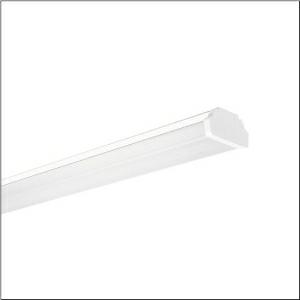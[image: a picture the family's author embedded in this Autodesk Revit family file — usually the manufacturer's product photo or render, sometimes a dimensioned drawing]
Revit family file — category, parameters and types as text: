
# Revit family: dus_31_gen_2_53bd812cv685c2_b411
name_source: partatom
category: Lighting Fixtures
units: mm (PartAtom-declared; Revit-internal decimal feet)

## family parameters
Cut with Voids When Loaded = No
Host = Face
Light Source = No
Part Type = Normal
Room Calculation Point = No
Round Connector Dimension = Use Diameter
Shared = No

## types (1)
- --- (1 x LED, 8970 lm, 49.9 W, 6500K)
    Apparent Load = 50 VA
    CIE Flux Codes = 47 80 95 93 100
    Color Rendering = 80
    Color Temperature = 6500K
    Default Elevation = 1800 mm
    Description = DUS 31 Gen.2, luminaire insert, of sheet steel, coil coated, white, length: 1.535mm, width: 81mm, height: 90mm, 5x system unit, system units: 307mm, LED rated luminous flux: 8.970lm, light colour: 865, SDCM (Standard Deviation of Colour Matching)MacAdam ≤ 3 SDCM (initial), control gear: ON/OFF Multilumen, CLOi, with plug, 3-pole, with phase selection, mains connection: 220..240V, AC, 50/60Hz, start of lifetime: 50W, end of service life: 61W, through-wiring accessed according to module size, primary optical cover: cover, of PMMA, light emission: direct distribution, primary light characteristic: symmetric, protection rating (complete): IP20, protection rating (LED compartment): IP50, insulation class (complete): insulation class I (protective earthing), certification: CE, ENEC, VDE, UKCA, impact resistance: IK03, permissible ambient temperature for indoor applications: -35..+40°C, corresponds to IFS (International Featured Standards) requirements for safety and quality in the food industry, reducing of maximum allowable ambient temperature of 5°C with ceiling mounting, packaging unit: 1 piece
    Height = 95 mm
    Lamp = 1 x LED
    Lamp Light Flux = 8970 lm
    Lamp Power = 49.9 W
    Lamp count = 1
    Length = 1535 mm
    Luminous efficacy = 180 lm/W
    Manufacturer = Siteco
    ModVariant = No
    Model = 53BD812CV685C2
    Mounting Place = Ceiling
    Mounting Type = Pendant
    Number of Poles = 1
    OnlyDefault = Yes
    Power Factor = 1
    Product Name = DUS 31 Gen.2
    Product group = luminaire insert | ceiling pendant
    ProductGroupID = 901
    Protection Class = Protection class I
    Protection Degree = IP 20
    RLX_Detail_Level = 1
    RLX_Emergency_Light_Flux = 0 lm
    RLX_Emergency_Type = 0
    RLX_Emergency_Type_DB = No
    RlxData = <blob elided: 29897 chars, md5=21da4db4>
    Socket = socket
    Standby Power = 0 W
    System Light Flux = 8970 lm
    System Power = 50 W
    Type Comments = factory setting: luminous flux: 100 % | (A | C | E) | 116 mA
    Type Image = l_1319596.jpg
    URL = http://relux.com
    VarID = @adj_049675
    Voltage = 0 V
    Weight = 0.00 kg
    Width = 81 mm

## geometry (parser evidence)
native form markers: Blend x4, Sweep x12
no freeform markers — native parametric forms only
